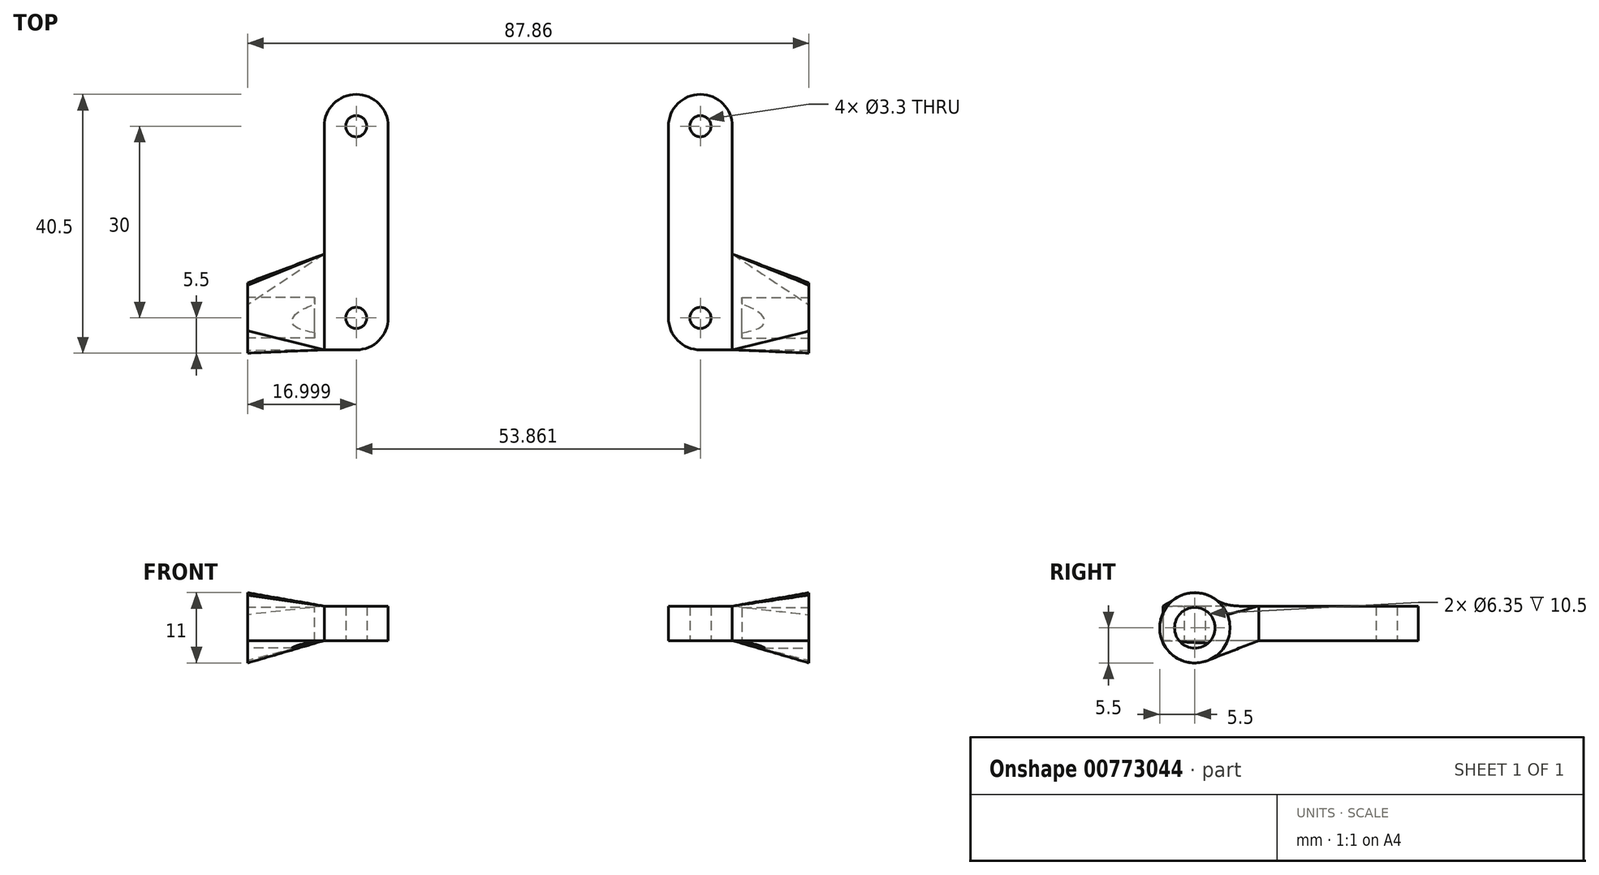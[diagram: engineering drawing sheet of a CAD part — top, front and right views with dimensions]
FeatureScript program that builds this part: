
annotation { "Feature Type Name" : "Feature", "Feature Type Description" : "" }
export const myFeature = defineFeature(function(context is Context, id is Id, definition is map)
    precondition{}
    {
        {
            var Q0;
            Q0=qCreatedBy(makeId("Top.planeOp"),FACE);
            var sketch = newSketch(context, id + "F0", { "sketchPlane" : qUnion([Q0])});
            skLineSegment(sketch, "E0.left", {"start": v(-6.93, 0.9) * mm, "end": v(-6.93, -29.1) * mm});
            skLineSegment(sketch, "E0.right", {"start": v(3.07, 0.9) * mm, "end": v(3.07, -29.1) * mm});
            skArc(sketch, "E1", {"start": v(3.07, -29.1) * mm, "mid": v(1.6, -32.64) * mm, "end": v(-1.93, -34.1) * mm});
            skLineSegment(sketch, "E2.top", {"start": v(-6.93, -34.1) * mm, "end": v(-1.93, -34.1) * mm});
            skLineSegment(sketch, "E2.left", {"start": v(-6.93, -29.1) * mm, "end": v(-6.93, -34.1) * mm});
            skCircle(sketch, "E3", {"center": v(-1.93, -29.1) * mm, "radius": 1.65 * mm});
            skArc(sketch, "E4", {"start": v(-6.93, 0.9) * mm, "mid": v(-1.93, 5.9) * mm, "end": v(3.07, 0.9) * mm});
            skCircle(sketch, "E5", {"center": v(-1.93, 0.9) * mm, "radius": 1.65 * mm});
            skSolve(sketch);
        }
        {
            var Q0;
            Q0 = qSketchRegion(id + "F0", true);
            extrude(context, id + "F1", {"entities" : qUnion([Q0]), "depth" : 5.4 * mm, "offsetDistance" : 25 * mm});
        }
        {
            var Q0;
            Q0=makeQuery(id+"F1.opExtrude","SWEPT_FACE",FACE,{"disambiguationData":[OSD([sQuery(id+"F0.wireOp",EDGE,"E0.left"),sQuery(id+"F0.wireOp",EDGE,"E2.left")])]});
            var sketch = newSketch(context, id + "F2", { "sketchPlane" : qUnion([Q0])});
            skLineSegment(sketch, "E6.bottom", {"start": v(34.1, 0) * mm, "end": v(19.1, 0) * mm});
            skLineSegment(sketch, "E6.top", {"start": v(34.1, 5.4) * mm, "end": v(19.1, 5.4) * mm});
            skLineSegment(sketch, "E6.left", {"start": v(34.1, 0) * mm, "end": v(34.1, 5.4) * mm});
            skLineSegment(sketch, "E6.right", {"start": v(19.1, 0) * mm, "end": v(19.1, 5.4) * mm});
            skSolve(sketch);
        }
        {
            var Q0;
            Q0=makeQuery(id+"F2.imprint","IMPRINT",FACE,{"disambiguationData":[TD([[makeQuery(id+"F2.imprint","IMPRINT",EDGE,{"derivedFrom":sQuery(id+"F2.wireOp",EDGE,"E6.bottom")}),1.0]])]});
            cPlane(context, id + "F3", {"entities" : qUnion([Q0]), "cplaneType" : CPlaneType.OFFSET, "offset" : 12 * mm, "width" : 150 * mm, "height" : 150 * mm});
        }
        {
            var Q0;
            Q0=qCreatedBy(id+"F3.planeOp",FACE);
            var sketch = newSketch(context, id + "F4", { "sketchPlane" : qUnion([Q0])});
            skCircle(sketch, "E7", {"center": v(29.1, 2) * mm, "radius": 3.18 * mm, "construction": true});
            skCircle(sketch, "E8", {"center": v(29.1, 2) * mm, "radius": 5.5 * mm});
            skLineSegment(sketch, "E9.0", {"start": v(27.45, 5.4) * mm, "end": v(30.75, 5.4) * mm, "construction": true});
            skLineSegment(sketch, "E10", {"start": v(29.1, 5.4) * mm, "end": v(29.1, -5.58) * mm, "construction": true});
            skSolve(sketch);
        }
        {
            var Q1;
            Q1=makeQuery(id+"F2.imprint","IMPRINT",FACE,{"disambiguationData":[TD([[makeQuery(id+"F2.imprint","IMPRINT",EDGE,{"derivedFrom":sQuery(id+"F2.wireOp",EDGE,"E6.bottom")}),1.0]])]});
            var Q2;
            Q2=makeQuery(id+"F4.imprint","IMPRINT",FACE,{"disambiguationData":[TD([[makeQuery(id+"F4.imprint","IMPRINT",EDGE,{"derivedFrom":sQuery(id+"F4.wireOp",EDGE,"E8")}),1.0]])]});
            loft(context, id + "F5", {"operationType" : NewBodyOperationType.ADD, "sheetProfilesArray" : [{ "sheetProfileEntities" : qUnion([Q1]) }, { "sheetProfileEntities" : qUnion([Q2]) }]});
        }
        {
            var Q0;
            Q0=makeQuery(id+"F5.opLoft","CAP_FACE",FACE,{"disambiguationData":[OSD([makeQuery(id+"F4.imprint","IMPRINT",FACE,{"disambiguationData":[TD([[makeQuery(id+"F4.imprint","IMPRINT",EDGE,{"derivedFrom":sQuery(id+"F4.wireOp",EDGE,"E8")}),1.0]])]})])],"isStart":true});
            var sketch = newSketch(context, id + "F6", { "sketchPlane" : qUnion([Q0])});
            skLineSegment(sketch, "E11", {"start": v(27.06, -3.1) * mm, "end": v(31.14, 7.1) * mm});
            skLineSegment(sketch, "E12", {"start": v(24, 4.04) * mm, "end": v(34.2, -0.04) * mm});
            skCircle(sketch, "E13", {"center": v(29.1, 2) * mm, "radius": 3.18 * mm});
            skSolve(sketch);
        }
        {
            var Q0;
            Q0 = qSketchRegion(id + "F6", true);
            extrude(context, id + "F7", {"entities" : qUnion([Q0]), "operationType" : NewBodyOperationType.REMOVE, "oppositeDirection" : true, "depth" : 10.5 * mm, "offsetDistance" : 25 * mm});
        }
        {
            var Q0;
            Q0=qCreatedBy(makeId("Right.planeOp"),FACE);
            cPlane(context, id + "F8", {"entities" : qUnion([Q0]), "cplaneType" : CPlaneType.OFFSET, "offset" : 25 * mm, "width" : 150 * mm, "height" : 150 * mm});
        }
        {
            var Q0;
            Q0=makeQuery(id+"F1.opExtrude","SWEPT_BODY",BODY,{"disambiguationData":[OSD([sQuery(id+"F0.wireOp",EDGE,"E0.left"),sQuery(id+"F0.wireOp",EDGE,"E0.right"),sQuery(id+"F0.wireOp",EDGE,"E1"),sQuery(id+"F0.wireOp",EDGE,"E2.top"),sQuery(id+"F0.wireOp",EDGE,"E2.left"),sQuery(id+"F0.wireOp",EDGE,"E3"),sQuery(id+"F0.wireOp",EDGE,"E4"),sQuery(id+"F0.wireOp",EDGE,"E5")])]});
            var Q1;
            Q1=qCreatedBy(id+"F8.planeOp",FACE);
            mirror(context, id + "F9", {"entities" : qUnion([Q0]), "mirrorPlane" : qUnion([Q1])});
        }
    });
